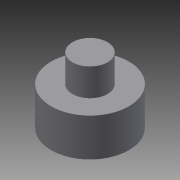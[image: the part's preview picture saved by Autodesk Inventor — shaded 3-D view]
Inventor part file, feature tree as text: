
AUTODESK INVENTOR PART (.ipt)
format: ipt  version: 2015 (Build 190159000, 159)  size: 94,208 bytes
history: native  units: mm
features: sketch x3, extrude x2, plane x1, hole x1
ambient origin geometry x8: Origin, YZ Plane, XZ Plane, XY Plane, X Axis, Y Axis, Z Axis, Center Point
bodies: Solid1 (feature_tree)
feature tree (7):
  extrude  "Extrusion1"  Depth=6.5mm TaperAngle=0.0deg
  plane  "Work Plane1"
  hole  "Hole1"  [1 undecoded]
  extrude  "Extrusion3"  Depth=4.7mm TaperAngle=0.0deg
  sketch  "Sketch1"  dims[d0=13.3mm d1=6.5mm d2=0.0mm]
  sketch  "Sketch3"  dims[d9=2.4mm]
  sketch  "Sketch4"  dims[d10=2.459mm d11=6.65mm d12=4.0mm d13=2.0mm d14=90.0deg d15=6.65mm d16=0.0mm d17=6.0mm d18=4.7mm d19=0.0mm]
note: 1 required parameter value undecoded (feature->parameter linkage not recoverable at this tier; creation-order binding heuristic only, values carry confidence <= 0.55)
